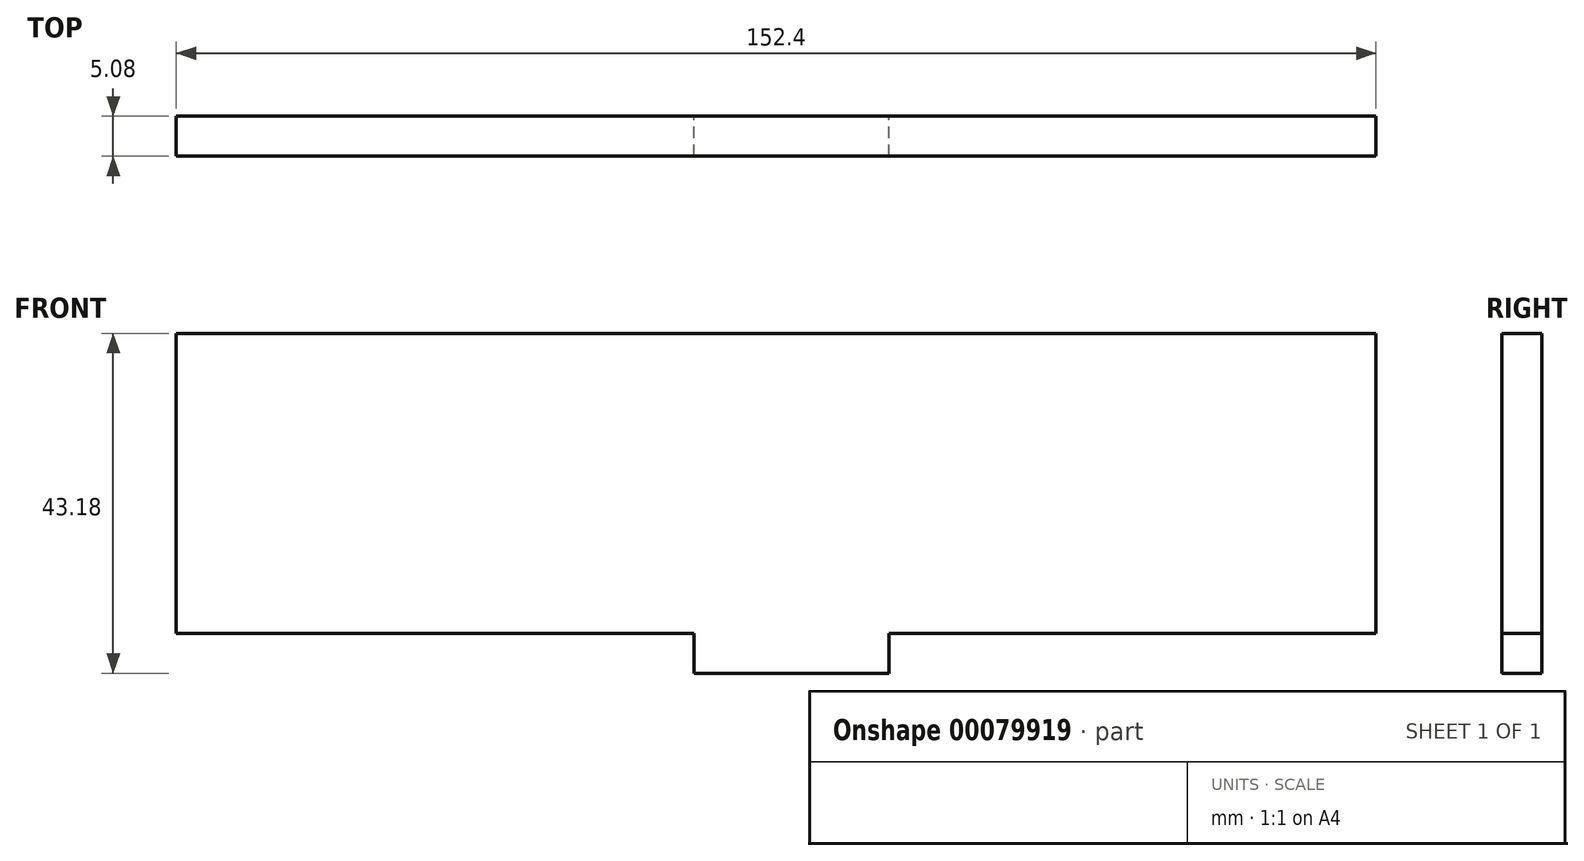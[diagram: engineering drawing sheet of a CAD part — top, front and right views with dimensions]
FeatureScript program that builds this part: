
annotation { "Feature Type Name" : "Feature", "Feature Type Description" : "" }
export const myFeature = defineFeature(function(context is Context, id is Id, definition is map)
    precondition{}
    {
        {
            var Q0;
            Q0=qCreatedBy(makeId("Front.planeOp"),FACE);
            var sketch = newSketch(context, id + "F0", { "sketchPlane" : qUnion([Q0])});
            skLineSegment(sketch, "E0.bottom", {"start": v(76.2, -19.05) * mm, "end": v(-76.2, -19.05) * mm});
            skLineSegment(sketch, "E0.top", {"start": v(76.2, 19.05) * mm, "end": v(-76.2, 19.05) * mm});
            skLineSegment(sketch, "E0.left", {"start": v(76.2, -19.05) * mm, "end": v(76.2, 19.05) * mm});
            skLineSegment(sketch, "E0.right", {"start": v(-76.2, -19.05) * mm, "end": v(-76.2, 19.05) * mm});
            skPoint(sketch, "E0.middle", {"position": v(0, 0) * mm});
            skLineSegment(sketch, "E1.bottom", {"start": v(-60.96, 19.05) * mm, "end": v(-39.76, 19.05) * mm});
            skLineSegment(sketch, "E1.top", {"start": v(-60.96, 24.13) * mm, "end": v(-39.76, 24.13) * mm});
            skLineSegment(sketch, "E1.left", {"start": v(-60.96, 19.05) * mm, "end": v(-60.96, 24.13) * mm});
            skLineSegment(sketch, "E1.right", {"start": v(-39.76, 19.05) * mm, "end": v(-39.76, 24.13) * mm});
            skLineSegment(sketch, "E2.bottom", {"start": v(-14.36, 19.05) * mm, "end": v(10.44, 19.05) * mm});
            skLineSegment(sketch, "E2.top", {"start": v(-14.36, 24.13) * mm, "end": v(10.44, 24.13) * mm});
            skLineSegment(sketch, "E2.left", {"start": v(-14.36, 19.05) * mm, "end": v(-14.36, 24.13) * mm});
            skLineSegment(sketch, "E2.right", {"start": v(10.44, 19.05) * mm, "end": v(10.44, 24.13) * mm});
            skLineSegment(sketch, "E3.bottom", {"start": v(35.84, 19.05) * mm, "end": v(60.96, 19.05) * mm});
            skLineSegment(sketch, "E3.top", {"start": v(35.84, 24.13) * mm, "end": v(60.96, 24.13) * mm});
            skLineSegment(sketch, "E3.left", {"start": v(35.84, 19.05) * mm, "end": v(35.84, 24.13) * mm});
            skLineSegment(sketch, "E3.right", {"start": v(60.96, 19.05) * mm, "end": v(60.96, 24.13) * mm});
            skLineSegment(sketch, "E4", {"start": v(-76.2, 0) * mm, "end": v(76.2, 0) * mm, "construction": true});
            skLineSegment(sketch, "E5.MirrorCS", {"start": v(-10.44, -19.05) * mm, "end": v(-10.44, -24.13) * mm});
            skLineSegment(sketch, "E6.MirrorCS", {"start": v(14.35, -19.05) * mm, "end": v(14.35, -24.13) * mm});
            skLineSegment(sketch, "E7.bottom", {"start": v(39.75, -19.05) * mm, "end": v(60.96, -19.05) * mm});
            skLineSegment(sketch, "E7.top", {"start": v(39.75, -24.13) * mm, "end": v(60.96, -24.13) * mm});
            skLineSegment(sketch, "E7.left", {"start": v(39.75, -19.05) * mm, "end": v(39.75, -24.13) * mm});
            skLineSegment(sketch, "E7.right", {"start": v(60.96, -19.05) * mm, "end": v(60.96, -24.13) * mm});
            skLineSegment(sketch, "E8.bottom", {"start": v(-35.84, -19.05) * mm, "end": v(-60.96, -19.05) * mm});
            skLineSegment(sketch, "E8.top", {"start": v(-35.84, -24.13) * mm, "end": v(-60.96, -24.13) * mm});
            skLineSegment(sketch, "E8.left", {"start": v(-35.84, -19.05) * mm, "end": v(-35.84, -24.13) * mm});
            skLineSegment(sketch, "E8.right", {"start": v(-60.96, -19.05) * mm, "end": v(-60.96, -24.13) * mm});
            skLineSegment(sketch, "E9", {"start": v(-10.44, -24.13) * mm, "end": v(14.35, -24.13) * mm});
            skSolve(sketch);
        }
        {
            var Q0;
            {var subQ0=sQuery(id+"F0.wireOp",EDGE,"E0.left");Q0=makeQuery(id+"F0.imprint","IMPRINT",FACE,{"disambiguationData":[TD([[makeQuery(id+"F0.imprint","IMPRINT",EDGE,{"derivedFrom":subQ0}),1.0]])]});}
            var Q1;
            Q1=makeQuery(id+"F0.imprint","IMPRINT",FACE,{"disambiguationData":[TD([[makeQuery(id+"F0.imprint","IMPRINT",EDGE,{"derivedFrom":sQuery(id+"F0.wireOp",EDGE,"E1.bottom")}),1.0]])]});
            var Q2;
            Q2=makeQuery(id+"F0.imprint","IMPRINT",FACE,{"disambiguationData":[TD([[makeQuery(id+"F0.imprint","IMPRINT",EDGE,{"derivedFrom":sQuery(id+"F0.wireOp",EDGE,"E2.bottom")}),1.0]])]});
            var Q3;
            Q3=makeQuery(id+"F0.imprint","IMPRINT",FACE,{"disambiguationData":[TD([[makeQuery(id+"F0.imprint","IMPRINT",EDGE,{"derivedFrom":sQuery(id+"F0.wireOp",EDGE,"E3.bottom")}),1.0]])]});
            var Q4;
            {var subQ0=sQuery(id+"F0.wireOp",EDGE,"4949790f-e6c9-4d1a-95bd-e3a7ba79d3f90.MirrorCS");Q4=makeQuery(id+"F0.imprint","IMPRINT",FACE,{"disambiguationData":[TD([[makeQuery(id+"F0.imprint","IMPRINT",EDGE,{"derivedFrom":subQ0}),1.0]])]});}
            var Q5;
            {var subQ0=sQuery(id+"F0.wireOp",EDGE,"E5.MirrorCS");Q5=makeQuery(id+"F0.imprint","IMPRINT",FACE,{"disambiguationData":[TD([[makeQuery(id+"F0.imprint","IMPRINT",EDGE,{"derivedFrom":subQ0}),1.0]])]});}
            var Q6;
            Q6=makeQuery(id+"F0.imprint","IMPRINT",FACE,{"disambiguationData":[TD([[makeQuery(id+"F0.imprint","IMPRINT",EDGE,{"derivedFrom":sQuery(id+"F0.wireOp",EDGE,"ec3a5fa8-0e76-499f-a8d0-41cd3bb077e30.MirrorCS")}),1.0]])]});
            var Q7;
            Q7=makeQuery(id+"F0.imprint","IMPRINT",FACE,{"disambiguationData":[TD([[makeQuery(id+"F0.imprint","IMPRINT",EDGE,{"derivedFrom":sQuery(id+"F0.wireOp",EDGE,"E7.bottom")}),-1.0]])]});
            var Q8;
            Q8=makeQuery(id+"F0.imprint","IMPRINT",FACE,{"disambiguationData":[TD([[makeQuery(id+"F0.imprint","IMPRINT",EDGE,{"derivedFrom":sQuery(id+"F0.wireOp",EDGE,"E8.bottom")}),1.0]])]});
            extrude(context, id + "F1", {"entities" : qUnion([Q0, Q1, Q2, Q3, Q4, Q5, Q6, Q7, Q8]), "depth" : 5.08 * mm});
        }
    });
